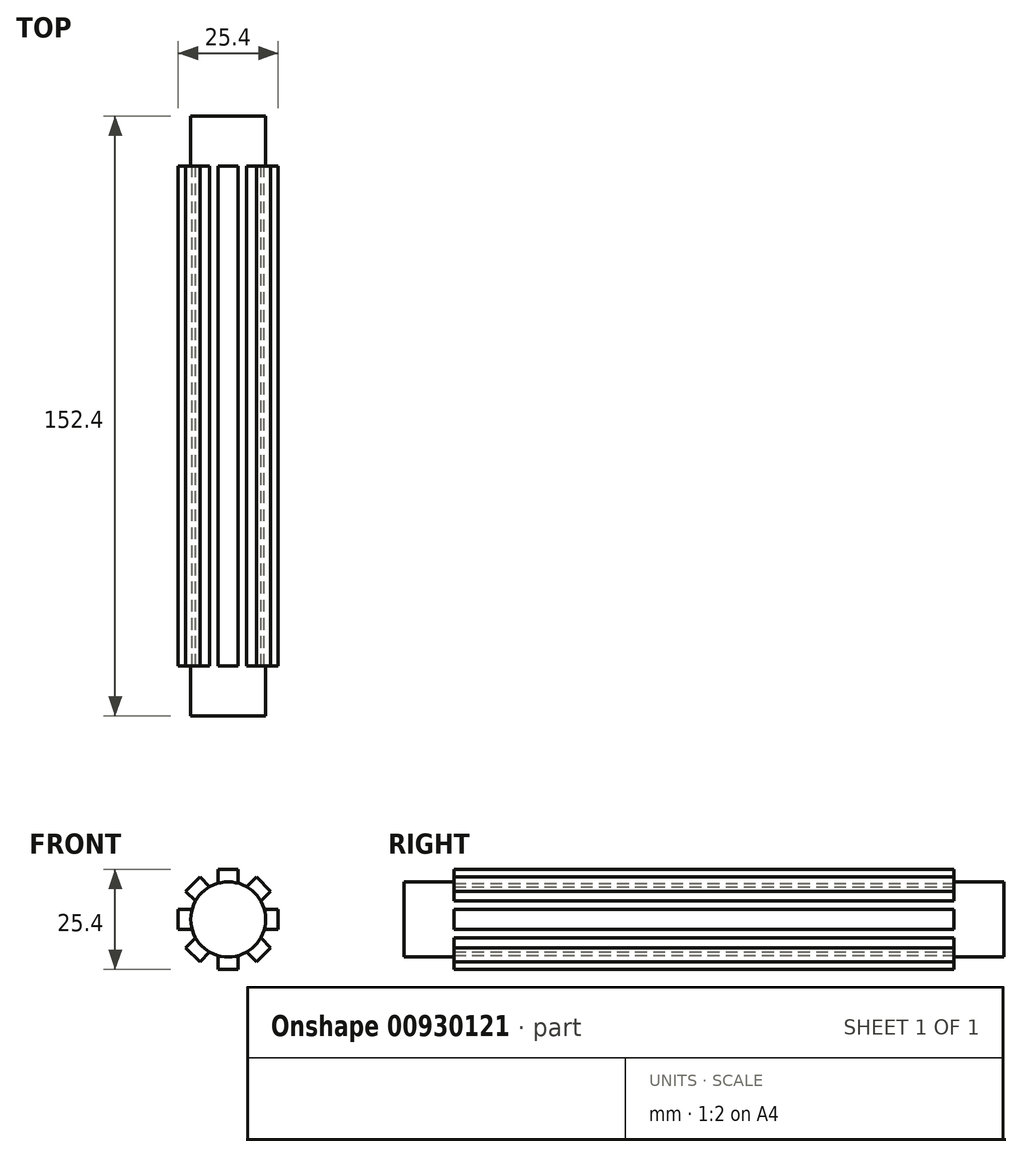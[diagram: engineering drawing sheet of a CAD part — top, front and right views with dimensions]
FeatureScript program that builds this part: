
annotation { "Feature Type Name" : "Feature", "Feature Type Description" : "" }
export const myFeature = defineFeature(function(context is Context, id is Id, definition is map)
    precondition{}
    {
        {
            var Q0;
            Q0=qCreatedBy(makeId("Front.planeOp"),FACE);
            var sketch = newSketch(context, id + "F0", { "sketchPlane" : qUnion([Q0])});
            skLineSegment(sketch, "E0.bottom", {"start": v(-2.54, 12.7) * mm, "end": v(2.54, 12.7) * mm});
            skLineSegment(sketch, "E0.top", {"start": v(-2.54, -12.7) * mm, "end": v(2.54, -12.7) * mm});
            skLineSegment(sketch, "E0.left", {"start": v(-2.54, 12.7) * mm, "end": v(-2.54, 9.18) * mm});
            skLineSegment(sketch, "E0.right", {"start": v(2.54, 12.7) * mm, "end": v(2.54, 9.18) * mm});
            skPoint(sketch, "E0.middle", {"position": v(0, 0) * mm});
            skLineSegment(sketch, "E1.bottom", {"start": v(-12.7, 2.54) * mm, "end": v(-9.18, 2.54) * mm});
            skLineSegment(sketch, "E1.top", {"start": v(-12.7, -2.54) * mm, "end": v(-9.18, -2.54) * mm});
            skLineSegment(sketch, "E1.left", {"start": v(-12.7, 2.54) * mm, "end": v(-12.7, -2.54) * mm});
            skLineSegment(sketch, "E1.right", {"start": v(12.7, 2.54) * mm, "end": v(12.7, -2.54) * mm});
            skLineSegment(sketch, "E2", {"start": v(8.98, 8.98) * mm, "end": v(7.18, 10.78) * mm});
            skLineSegment(sketch, "E3.MirrorCS", {"start": v(8.98, 8.98) * mm, "end": v(10.78, 7.18) * mm});
            skLineSegment(sketch, "E4.MirrorCS", {"start": v(-8.98, -8.98) * mm, "end": v(-7.18, -10.78) * mm});
            skLineSegment(sketch, "E5.MirrorCS", {"start": v(-8.98, -8.98) * mm, "end": v(-10.78, -7.18) * mm});
            skLineSegment(sketch, "E6", {"start": v(7.18, 10.78) * mm, "end": v(4.7, 8.29) * mm});
            skLineSegment(sketch, "E7", {"start": v(-7.18, -10.78) * mm, "end": v(-4.7, -8.29) * mm});
            skLineSegment(sketch, "E8", {"start": v(8.98, -8.98) * mm, "end": v(7.18, -10.78) * mm});
            skLineSegment(sketch, "E9.MirrorCS", {"start": v(-8.98, 8.98) * mm, "end": v(-10.78, 7.18) * mm});
            skLineSegment(sketch, "E10.MirrorCS", {"start": v(8.98, -8.98) * mm, "end": v(10.78, -7.18) * mm});
            skLineSegment(sketch, "E11.MirrorCS", {"start": v(-8.98, 8.98) * mm, "end": v(-7.18, 10.78) * mm});
            skLineSegment(sketch, "E12", {"start": v(-7.18, 10.78) * mm, "end": v(-4.7, 8.29) * mm});
            skLineSegment(sketch, "E13", {"start": v(7.18, -10.78) * mm, "end": v(4.7, -8.29) * mm});
            skArc(sketch, "E14", {"start": v(-8.29, 4.7) * mm, "mid": v(-8.8, 3.65) * mm, "end": v(-9.18, 2.54) * mm});
            skLineSegment(sketch, "E15.trimOffspring", {"start": v(-8.29, -4.7) * mm, "end": v(-10.78, -7.18) * mm});
            skLineSegment(sketch, "E16.trimOffspring", {"start": v(-8.29, 4.7) * mm, "end": v(-10.78, 7.18) * mm});
            skPoint(sketch, "E17.orphan", {"position": v(-8.98, 8.98) * mm});
            skArc(sketch, "E18.trimOffspring", {"start": v(-2.54, 9.18) * mm, "mid": v(-3.65, 8.8) * mm, "end": v(-4.7, 8.29) * mm});
            skLineSegment(sketch, "E19.trimOffspring", {"start": v(-2.54, -9.18) * mm, "end": v(-2.54, -12.7) * mm});
            skArc(sketch, "E20.trimOffspring", {"start": v(2.54, -9.18) * mm, "mid": v(3.65, -8.8) * mm, "end": v(4.7, -8.29) * mm});
            skArc(sketch, "E21.trimOffspring", {"start": v(-4.7, -8.29) * mm, "mid": v(-3.65, -8.8) * mm, "end": v(-2.54, -9.18) * mm});
            skArc(sketch, "E22.trimOffspring", {"start": v(-9.18, -2.54) * mm, "mid": v(-8.8, -3.65) * mm, "end": v(-8.29, -4.7) * mm});
            skArc(sketch, "E23.trimOffspring", {"start": v(4.7, 8.29) * mm, "mid": v(3.65, 8.8) * mm, "end": v(2.54, 9.18) * mm});
            skArc(sketch, "E24.trimOffspring", {"start": v(9.18, 2.54) * mm, "mid": v(8.8, 3.65) * mm, "end": v(8.29, 4.7) * mm});
            skLineSegment(sketch, "E25.trimOffspring", {"start": v(8.29, 4.7) * mm, "end": v(10.78, 7.18) * mm});
            skLineSegment(sketch, "E26.trimOffspring", {"start": v(2.54, -9.18) * mm, "end": v(2.54, -12.7) * mm});
            skArc(sketch, "E27.trimOffspring", {"start": v(8.29, -4.7) * mm, "mid": v(8.8, -3.65) * mm, "end": v(9.18, -2.54) * mm});
            skLineSegment(sketch, "E28.trimOffspring", {"start": v(8.29, -4.7) * mm, "end": v(10.78, -7.18) * mm});
            skLineSegment(sketch, "E29.trimOffspring", {"start": v(9.18, -2.54) * mm, "end": v(12.7, -2.54) * mm});
            skLineSegment(sketch, "E30.trimOffspring", {"start": v(9.18, 2.54) * mm, "end": v(12.7, 2.54) * mm});
            skSolve(sketch);
        }
        {
            var Q0;
            Q0=makeQuery(id+"F0.imprint","IMPRINT",FACE,{"disambiguationData":[TD([[makeQuery(id+"F0.imprint","IMPRINT",EDGE,{"derivedFrom":sQuery(id+"F0.wireOp",EDGE,"E0.bottom")}),-1.0]])]});
            extrude(context, id + "F1", {"entities" : qUnion([Q0]), "depth" : 127 * mm, "offsetDistance" : 25.4 * mm});
        }
        {
            var Q0;
            Q0=makeQuery(id+"F1.opExtrude","CAP_FACE",FACE,{"disambiguationData":[OSD([sQuery(id+"F0.wireOp",EDGE,"E0.bottom"),sQuery(id+"F0.wireOp",EDGE,"E0.top"),sQuery(id+"F0.wireOp",EDGE,"E0.left"),sQuery(id+"F0.wireOp",EDGE,"E0.right"),sQuery(id+"F0.wireOp",EDGE,"E1.bottom"),sQuery(id+"F0.wireOp",EDGE,"E1.top"),sQuery(id+"F0.wireOp",EDGE,"E1.left"),sQuery(id+"F0.wireOp",EDGE,"E1.right"),sQuery(id+"F0.wireOp",EDGE,"E2"),sQuery(id+"F0.wireOp",EDGE,"E3.MirrorCS"),sQuery(id+"F0.wireOp",EDGE,"E4.MirrorCS"),sQuery(id+"F0.wireOp",EDGE,"E5.MirrorCS"),sQuery(id+"F0.wireOp",EDGE,"E6"),sQuery(id+"F0.wireOp",EDGE,"E7"),sQuery(id+"F0.wireOp",EDGE,"E8"),sQuery(id+"F0.wireOp",EDGE,"E9.MirrorCS"),sQuery(id+"F0.wireOp",EDGE,"E10.MirrorCS"),sQuery(id+"F0.wireOp",EDGE,"E11.MirrorCS"),sQuery(id+"F0.wireOp",EDGE,"E12"),sQuery(id+"F0.wireOp",EDGE,"E13"),sQuery(id+"F0.wireOp",EDGE,"E14"),sQuery(id+"F0.wireOp",EDGE,"E15.trimOffspring"),sQuery(id+"F0.wireOp",EDGE,"E16.trimOffspring"),sQuery(id+"F0.wireOp",EDGE,"E18.trimOffspring"),sQuery(id+"F0.wireOp",EDGE,"E19.trimOffspring"),sQuery(id+"F0.wireOp",EDGE,"E20.trimOffspring"),sQuery(id+"F0.wireOp",EDGE,"E21.trimOffspring"),sQuery(id+"F0.wireOp",EDGE,"E22.trimOffspring"),sQuery(id+"F0.wireOp",EDGE,"E23.trimOffspring"),sQuery(id+"F0.wireOp",EDGE,"E24.trimOffspring"),sQuery(id+"F0.wireOp",EDGE,"E25.trimOffspring"),sQuery(id+"F0.wireOp",EDGE,"E26.trimOffspring"),sQuery(id+"F0.wireOp",EDGE,"E27.trimOffspring"),sQuery(id+"F0.wireOp",EDGE,"E28.trimOffspring"),sQuery(id+"F0.wireOp",EDGE,"E29.trimOffspring"),sQuery(id+"F0.wireOp",EDGE,"E30.trimOffspring")])],"isStart":false});
            var sketch = newSketch(context, id + "F2", { "sketchPlane" : qUnion([Q0])});
            skCircle(sketch, "E31", {"center": v(0, 0) * mm, "radius": 9.53 * mm});
            skSolve(sketch);
        }
        {
            var Q0;
            Q0 = qSketchRegion(id + "F2", true);
            extrude(context, id + "F3", {"entities" : qUnion([Q0]), "operationType" : NewBodyOperationType.ADD, "depth" : 12.7 * mm, "offsetDistance" : 25.4 * mm});
        }
        {
            var Q0;
            Q0=makeQuery(id+"F1.opExtrude","CAP_FACE",FACE,{"disambiguationData":[OSD([sQuery(id+"F0.wireOp",EDGE,"E0.bottom"),sQuery(id+"F0.wireOp",EDGE,"E0.top"),sQuery(id+"F0.wireOp",EDGE,"E0.left"),sQuery(id+"F0.wireOp",EDGE,"E0.right"),sQuery(id+"F0.wireOp",EDGE,"E1.bottom"),sQuery(id+"F0.wireOp",EDGE,"E1.top"),sQuery(id+"F0.wireOp",EDGE,"E1.left"),sQuery(id+"F0.wireOp",EDGE,"E1.right"),sQuery(id+"F0.wireOp",EDGE,"E2"),sQuery(id+"F0.wireOp",EDGE,"E3.MirrorCS"),sQuery(id+"F0.wireOp",EDGE,"E4.MirrorCS"),sQuery(id+"F0.wireOp",EDGE,"E5.MirrorCS"),sQuery(id+"F0.wireOp",EDGE,"E6"),sQuery(id+"F0.wireOp",EDGE,"E7"),sQuery(id+"F0.wireOp",EDGE,"E8"),sQuery(id+"F0.wireOp",EDGE,"E9.MirrorCS"),sQuery(id+"F0.wireOp",EDGE,"E10.MirrorCS"),sQuery(id+"F0.wireOp",EDGE,"E11.MirrorCS"),sQuery(id+"F0.wireOp",EDGE,"E12"),sQuery(id+"F0.wireOp",EDGE,"E13"),sQuery(id+"F0.wireOp",EDGE,"E14"),sQuery(id+"F0.wireOp",EDGE,"E15.trimOffspring"),sQuery(id+"F0.wireOp",EDGE,"E16.trimOffspring"),sQuery(id+"F0.wireOp",EDGE,"E18.trimOffspring"),sQuery(id+"F0.wireOp",EDGE,"E19.trimOffspring"),sQuery(id+"F0.wireOp",EDGE,"E20.trimOffspring"),sQuery(id+"F0.wireOp",EDGE,"E21.trimOffspring"),sQuery(id+"F0.wireOp",EDGE,"E22.trimOffspring"),sQuery(id+"F0.wireOp",EDGE,"E23.trimOffspring"),sQuery(id+"F0.wireOp",EDGE,"E24.trimOffspring"),sQuery(id+"F0.wireOp",EDGE,"E25.trimOffspring"),sQuery(id+"F0.wireOp",EDGE,"E26.trimOffspring"),sQuery(id+"F0.wireOp",EDGE,"E27.trimOffspring"),sQuery(id+"F0.wireOp",EDGE,"E28.trimOffspring"),sQuery(id+"F0.wireOp",EDGE,"E29.trimOffspring"),sQuery(id+"F0.wireOp",EDGE,"E30.trimOffspring")])],"isStart":true});
            var sketch = newSketch(context, id + "F4", { "sketchPlane" : qUnion([Q0])});
            skCircle(sketch, "E32", {"center": v(0, 0) * mm, "radius": 9.53 * mm});
            skSolve(sketch);
        }
        {
            var Q0;
            {var subQ0=sQuery(id+"F4.wireOp",EDGE,"E32");var subQ4=makeQuery(id+"F4.imprint","INTERSECT",VERTEX,{"derivedFrom":[makeQuery(id+"F1.opExtrude","CAP_EDGE",EDGE,{"disambiguationData":[OSD([sQuery(id+"F0.wireOp",EDGE,"E16.trimOffspring")])],"isStart":true}),subQ0]});var subQ13=makeQuery(id+"F4.imprint","INTERSECT",VERTEX,{"derivedFrom":[makeQuery(id+"F1.opExtrude","CAP_EDGE",EDGE,{"disambiguationData":[OSD([sQuery(id+"F0.wireOp",EDGE,"E1.bottom")])],"isStart":true}),subQ0]});Q0=makeQuery(id+"F4.imprint","IMPRINT",FACE,{"disambiguationData":[TD([[makeQuery(id+"F4.imprint","IMPRINT",EDGE,{"disambiguationData":[TD([[subQ13,1.0],[subQ4,-1.0]])],"derivedFrom":subQ0}),-1.0]])]});}
            extrude(context, id + "F5", {"entities" : qUnion([Q0]), "operationType" : NewBodyOperationType.ADD, "depth" : 12.7 * mm, "offsetDistance" : 25.4 * mm});
        }
    });
